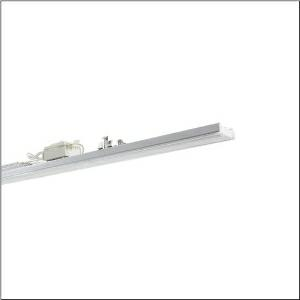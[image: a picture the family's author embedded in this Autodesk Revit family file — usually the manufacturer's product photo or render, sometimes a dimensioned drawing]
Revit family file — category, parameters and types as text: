
# Revit family: licross_r__11_recessed_extreme_mo_51te1edv4e5ge_7dbd
name_source: partatom
category: Lighting Fixtures
units: mm (PartAtom-declared; Revit-internal decimal feet)

## family parameters
Cut with Voids When Loaded = No
Host = Face
Light Source = No
Part Type = Normal
Room Calculation Point = No
Round Connector Dimension = Use Diameter
Shared = No

## types (1)
- --- (1 x LED, 14910 lm, 84.5 W, 4000K)
    Apparent Load = 85 VA
    CIE Flux Codes = 85 95 99 100 100
    Color Rendering = 80
    Color Temperature = 4000K
    Default Elevation = 1800 mm
    Description = Licross® 11 Recessed extreme MO, luminaire insert, of sheet steel, galvanised, coil coated, white, length: 2.250mm, width: 66mm, height: 67mm, LED rated luminous flux: 14.910lm, light colour: 840, control gear: DALI 2, with plug, 5-pole, with phase selection, mains connection: 220..240V, AC, 50/60Hz, rated input power: 85W, internal wiring halogen-free, primary light control with lens, of plastic, primary optical cover: cover, of PMMA, light emission: direct distribution, primary light characteristic: symmetric, protection rating (complete): IP54, insulation class (complete): insulation class I (protective earthing), certification: CE, ENEC, VDE, UKCA, protection symbol: D if used in an environment with non-conductive dust loads with corresponding accessories, impact resistance: IK06, permissible ambient temperature for indoor applications: -25..+45°C, corresponds to IFS (International Featured Standards) requirements for safety and quality in the food industry, reducing of maximum allowable ambient temperature of 5°C with ceiling mounting, LABS conformity tested according to VDMA 24364:2018-05, packaging unit: 1 piece
    Height = 58 mm
    Lamp = 1 x LED
    Lamp Light Flux = 14910 lm
    Lamp Power = 84.5 W
    Lamp count = 1
    Length = 2250 mm
    Luminous efficacy = 176 lm/W
    Manufacturer = Siteco
    ModVariant = No
    Model = 51TE1EDV4E5GE
    Mounting Place = Ceiling
    Mounting Type = Pendant
    Number of Poles = 1
    OnlyDefault = Yes
    Power Factor = 1
    Product Name = Licross® 11 Recessed extreme MO
    Product group = luminaire insert | ceiling pendant
    ProductGroupID = 902
    Protection Class = Protection class I
    Protection Degree = IP 54
    RLX_Detail_Level = 1
    RLX_Emergency_Light_Flux = 0 lm
    RLX_Emergency_Type = 0
    RLX_Emergency_Type_DB = No
    RlxData = <blob elided: 29749 chars, md5=f92e4571>
    Socket = socket
    Standby Power = 0 W
    System Light Flux = 14910 lm
    System Power = 85 W
    Type Comments = factory setting: luminous flux: 100 % | dim-lin: 254 | 380 mA
    Type Image = l_1296930.jpg
    URL = http://relux.com
    VarID = @adj_110925
    Voltage = 0 V
    Weight = 0.00 kg
    Width = 66 mm

## geometry (parser evidence)
native form markers: Blend x4, Sweep x10
no freeform markers — native parametric forms only
